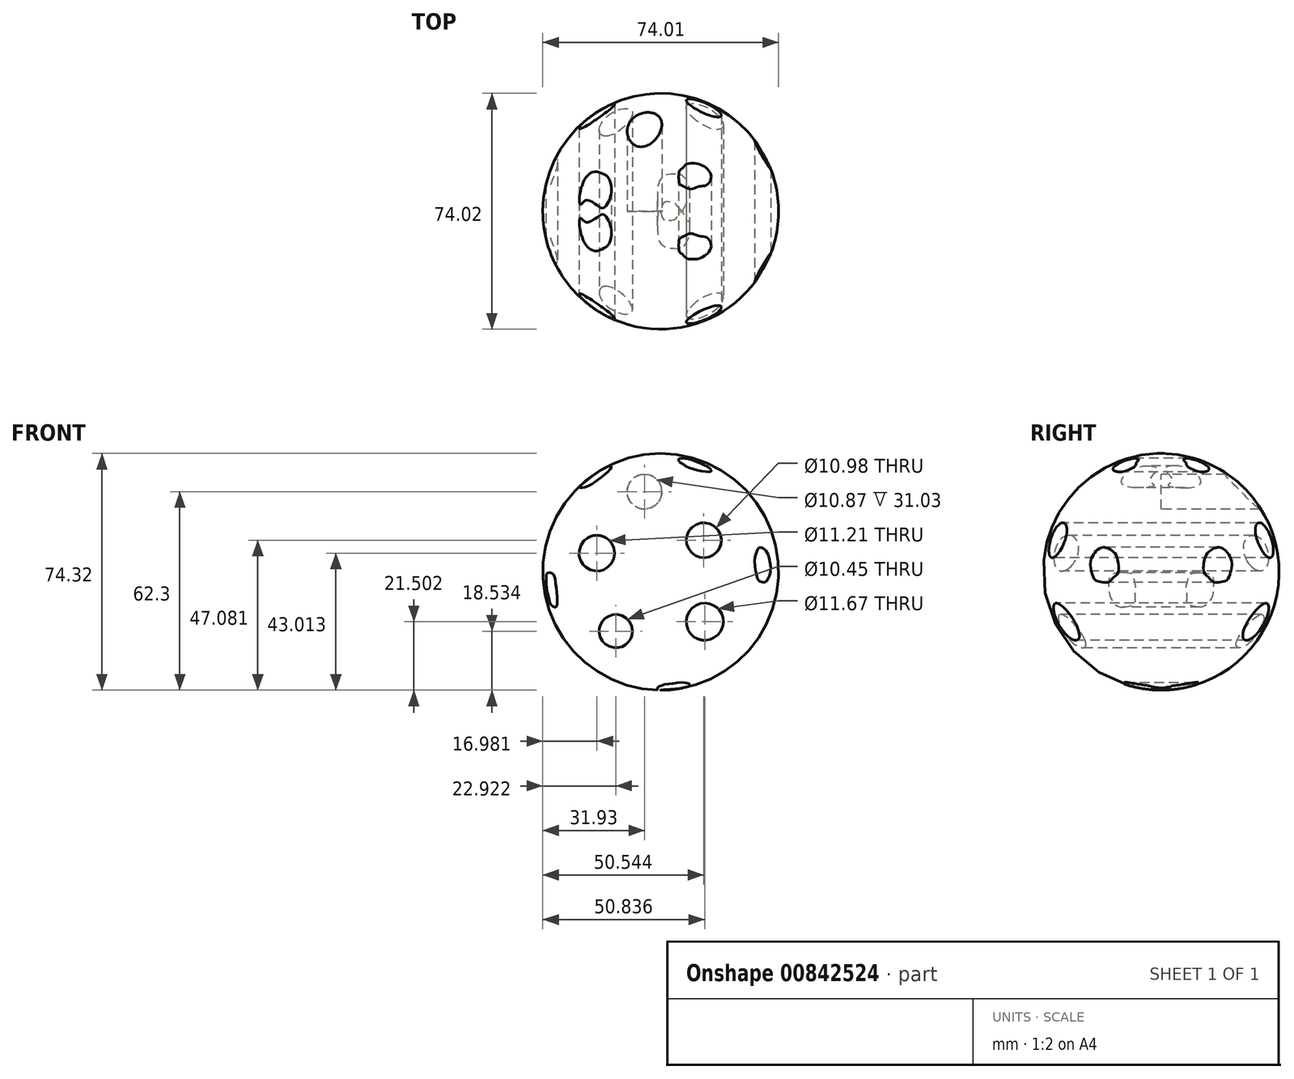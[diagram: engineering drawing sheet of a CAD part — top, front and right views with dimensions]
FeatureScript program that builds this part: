
annotation { "Feature Type Name" : "Feature", "Feature Type Description" : "" }
export const myFeature = defineFeature(function(context is Context, id is Id, definition is map)
    precondition{}
    {
        {
            var Q0;
            Q0=qCreatedBy(makeId("Front.planeOp"),FACE);
            var sketch = newSketch(context, id + "F0", { "sketchPlane" : qUnion([Q0])});
            skArc(sketch, "E0", {"start": v(-35.7, 11.6) * mm, "mid": v(-29.25, -20.64) * mm, "end": v(0.25, -35.18) * mm});
            skArc(sketch, "E1", {"start": v(0, 39.14) * mm, "mid": v(-36.88, 1.86) * mm, "end": v(0.25, -35.18) * mm});
            skLineSegment(sketch, "E2", {"start": v(0, 39.14) * mm, "end": v(0.25, -35.18) * mm});
            skSolve(sketch);
        }
        {
            var Q0;
            Q0=makeQuery(id+"F0.imprint","IMPRINT",FACE,{"disambiguationData":[TD([[makeQuery(id+"F0.imprint","IMPRINT",EDGE,{"derivedFrom":sQuery(id+"F0.wireOp",EDGE,"E1")}),1.0]])]});
            var Q1;
            Q1=sQuery(id+"F0.wireOp",EDGE,"E2");
            revolve(context, id + "F1", {"surfaceOperationType" : NewSurfaceOperationType.NEW, "entities" : qUnion([Q0]), "axis" : qUnion([Q1]), "revolveType" : RevolveType.FULL});
        }
        {
            var Q0;
            Q0=qCreatedBy(makeId("Front.planeOp"),FACE);
            var sketch = newSketch(context, id + "F2", { "sketchPlane" : qUnion([Q0])});
            skCircle(sketch, "E3", {"center": v(13.66, 11.9) * mm, "radius": 5.49 * mm});
            skSolve(sketch);
        }
        {
            var Q0;
            Q0 = qSketchRegion(id + "F2", true);
            extrude(context, id + "F3", {"entities" : qUnion([Q0]), "operationType" : NewBodyOperationType.ADD, "depth" : 56.6 * mm, "offsetDistance" : 25 * mm});
        }
        {
            var Q0;
            Q0=makeQuery(id+"F3.opExtrude","CAP_FACE",FACE,{"disambiguationData":[OSD([sQuery(id+"F2.wireOp",EDGE,"E3")])],"isStart":false});
            extrude(context, id + "F4", {"entities" : qUnion([Q0]), "operationType" : NewBodyOperationType.REMOVE, "oppositeDirection" : true, "depth" : 1000 * mm, "offsetDistance" : 25 * mm});
        }
        {
            var Q0;
            Q0=qCreatedBy(makeId("Front.planeOp"),FACE);
            var sketch = newSketch(context, id + "F5", { "sketchPlane" : qUnion([Q0])});
            skCircle(sketch, "E4", {"center": v(13.96, -13.68) * mm, "radius": 5.84 * mm});
            skCircle(sketch, "E5", {"center": v(-13.96, -16.65) * mm, "radius": 5.23 * mm});
            skCircle(sketch, "E6", {"center": v(-19.9, 7.83) * mm, "radius": 5.6 * mm});
            skCircle(sketch, "E7", {"center": v(-4.95, 27.12) * mm, "radius": 5.43 * mm});
            skSolve(sketch);
        }
        {
            var Q0;
            Q0 = qSketchRegion(id + "F5", true);
            extrude(context, id + "F6", {"entities" : qUnion([Q0]), "operationType" : NewBodyOperationType.REMOVE, "oppositeDirection" : true, "depth" : 1000 * mm, "offsetDistance" : 25 * mm});
        }
        {
            var Q0;
            Q0=qCreatedBy(makeId("Front.planeOp"),FACE);
            var sketch = newSketch(context, id + "F7", { "sketchPlane" : qUnion([Q0])});
            skFitSpline(sketch, "E8", {"points": [v(-35.4, 1.6) * mm, v(-35.84, 0.94) * mm, v(-35.84, 0) * mm, v(-35.77, -2.24) * mm, v(-35.54, -3.79) * mm, v(-35.25, -5.26) * mm, v(-34.73, -7.48) * mm, v(-34.14, -8.59) * mm, v(-32.88, -9.1) * mm, v(-32.37, -8.07) * mm, v(-32.44, -4.6) * mm, v(-32.81, -1.87) * mm, v(-33.62, 1.24) * mm, v(-35.4, 1.6) * mm]});
            skFitSpline(sketch, "E9", {"points": [v(31.77, 9.64) * mm, v(30.84, 9.38) * mm, v(30.13, 7.97) * mm, v(29.69, 6.26) * mm, v(29.65, 4.14) * mm, v(30.02, 1.9) * mm, v(30.76, -0.66) * mm, v(31.65, -1.18) * mm, v(32.96, -1.32) * mm, v(33.85, 0) * mm, v(34.55, 1.6) * mm, v(34.37, 5.59) * mm, v(33.36, 8.3) * mm, v(31.77, 9.64) * mm]});
            skFitSpline(sketch, "E10", {"points": [v(-0.86, -35.07) * mm, v(-0.52, -34.06) * mm, v(0.65, -33.6) * mm, v(1.83, -33.3) * mm, v(3.92, -33.05) * mm, v(5.35, -32.84) * mm, v(6.99, -32.72) * mm, v(9.13, -33.26) * mm, v(9.3, -33.77) * mm, v(8.62, -34.02) * mm, v(7.78, -34.31) * mm, v(5.9, -34.69) * mm, v(4.43, -34.81) * mm, v(3, -34.94) * mm, v(1.5, -35.02) * mm, v(0, -35.2) * mm, v(-0.86, -35.07) * mm]});
            skFitSpline(sketch, "E11", {"points": [v(5.88, 37.48) * mm, v(5.9, 36.49) * mm, v(7.12, 35.75) * mm, v(8.18, 35.05) * mm, v(10.3, 34.31) * mm, v(11.73, 33.87) * mm, v(13.87, 33.45) * mm, v(15.21, 33.32) * mm, v(15.98, 33.58) * mm, v(15.18, 34.73) * mm, v(12.72, 35.98) * mm, v(11.09, 36.65) * mm, v(8.98, 37.32) * mm, v(6.23, 37.6) * mm, v(5.88, 37.48) * mm]});
            skFitSpline(sketch, "E12", {"points": [v(-15.4, 35.15) * mm, v(-16.05, 33.79) * mm, v(-17.95, 32.15) * mm, v(-20.2, 30.35) * mm, v(-22.14, 29.16) * mm, v(-24.12, 28.44) * mm, v(-25.38, 28.58) * mm, v(-23.88, 30.04) * mm, v(-22, 31.54) * mm, v(-19.83, 33.18) * mm, v(-16.66, 34.98) * mm, v(-15.4, 35.15) * mm]});
            skSolve(sketch);
        }
        {
            var Q0;
            Q0 = qSketchRegion(id + "F7", true);
            extrude(context, id + "F8", {"entities" : qUnion([Q0]), "operationType" : NewBodyOperationType.ADD, "depth" : 1000 * mm, "offsetDistance" : 25 * mm});
        }
        {
            var Q0;
            Q0=makeQuery(id+"F8.opExtrude","CAP_FACE",FACE,{"disambiguationData":[OSD([sQuery(id+"F7.wireOp",EDGE,"E8")])],"isStart":false});
            var Q1;
            Q1=makeQuery(id+"F8.opExtrude","CAP_FACE",FACE,{"disambiguationData":[OSD([sQuery(id+"F7.wireOp",EDGE,"E12")])],"isStart":false});
            var Q2;
            Q2=makeQuery(id+"F8.opExtrude","CAP_FACE",FACE,{"disambiguationData":[OSD([sQuery(id+"F7.wireOp",EDGE,"E11")])],"isStart":false});
            var Q3;
            Q3=makeQuery(id+"F8.opExtrude","CAP_FACE",FACE,{"disambiguationData":[OSD([sQuery(id+"F7.wireOp",EDGE,"E9")])],"isStart":false});
            var Q4;
            Q4=makeQuery(id+"F8.opExtrude","CAP_FACE",FACE,{"disambiguationData":[OSD([sQuery(id+"F7.wireOp",EDGE,"E10")])],"isStart":false});
            extrude(context, id + "F9", {"entities" : qUnion([Q0, Q1, Q2, Q3, Q4]), "operationType" : NewBodyOperationType.REMOVE, "oppositeDirection" : true, "depth" : 2000 * mm, "offsetDistance" : 25 * mm});
        }
        {
            var Q0;
            Q0=makeQuery(id+"F6.boolean.opBoolean","COPY",FACE,{"derivedFrom":makeQuery(id+"F6.opExtrude","CAP_FACE",FACE,{"disambiguationData":[OSD([sQuery(id+"F5.wireOp",EDGE,"E6")])],"isStart":true})});
            extrude(context, id + "F10", {"entities" : qUnion([Q0]), "operationType" : NewBodyOperationType.REMOVE, "oppositeDirection" : true, "depth" : 1000 * mm, "offsetDistance" : 25 * mm});
        }
        {
            var Q0;
            Q0=makeQuery(id+"F6.boolean.opBoolean","COPY",FACE,{"derivedFrom":makeQuery(id+"F6.opExtrude","CAP_FACE",FACE,{"disambiguationData":[OSD([sQuery(id+"F5.wireOp",EDGE,"E4")])],"isStart":true})});
            extrude(context, id + "F11", {"entities" : qUnion([Q0]), "operationType" : NewBodyOperationType.REMOVE, "oppositeDirection" : true, "depth" : 1000 * mm, "offsetDistance" : 25 * mm});
        }
        {
            var Q0;
            Q0=makeQuery(id+"F6.boolean.opBoolean","COPY",FACE,{"derivedFrom":makeQuery(id+"F6.opExtrude","CAP_FACE",FACE,{"disambiguationData":[OSD([sQuery(id+"F5.wireOp",EDGE,"E5")])],"isStart":true})});
            extrude(context, id + "F12", {"entities" : qUnion([Q0]), "operationType" : NewBodyOperationType.REMOVE, "depth" : 1000 * mm, "offsetDistance" : 25 * mm});
        }
        {
            var Q0;
            Q0=makeQuery(id+"F6.boolean.opBoolean","COPY",FACE,{"derivedFrom":makeQuery(id+"F6.opExtrude","CAP_FACE",FACE,{"disambiguationData":[OSD([sQuery(id+"F5.wireOp",EDGE,"E5")])],"isStart":true})});
            extrude(context, id + "F13", {"entities" : qUnion([Q0]), "operationType" : NewBodyOperationType.REMOVE, "oppositeDirection" : true, "depth" : 10000 * mm, "offsetDistance" : 25 * mm});
        }
    });
